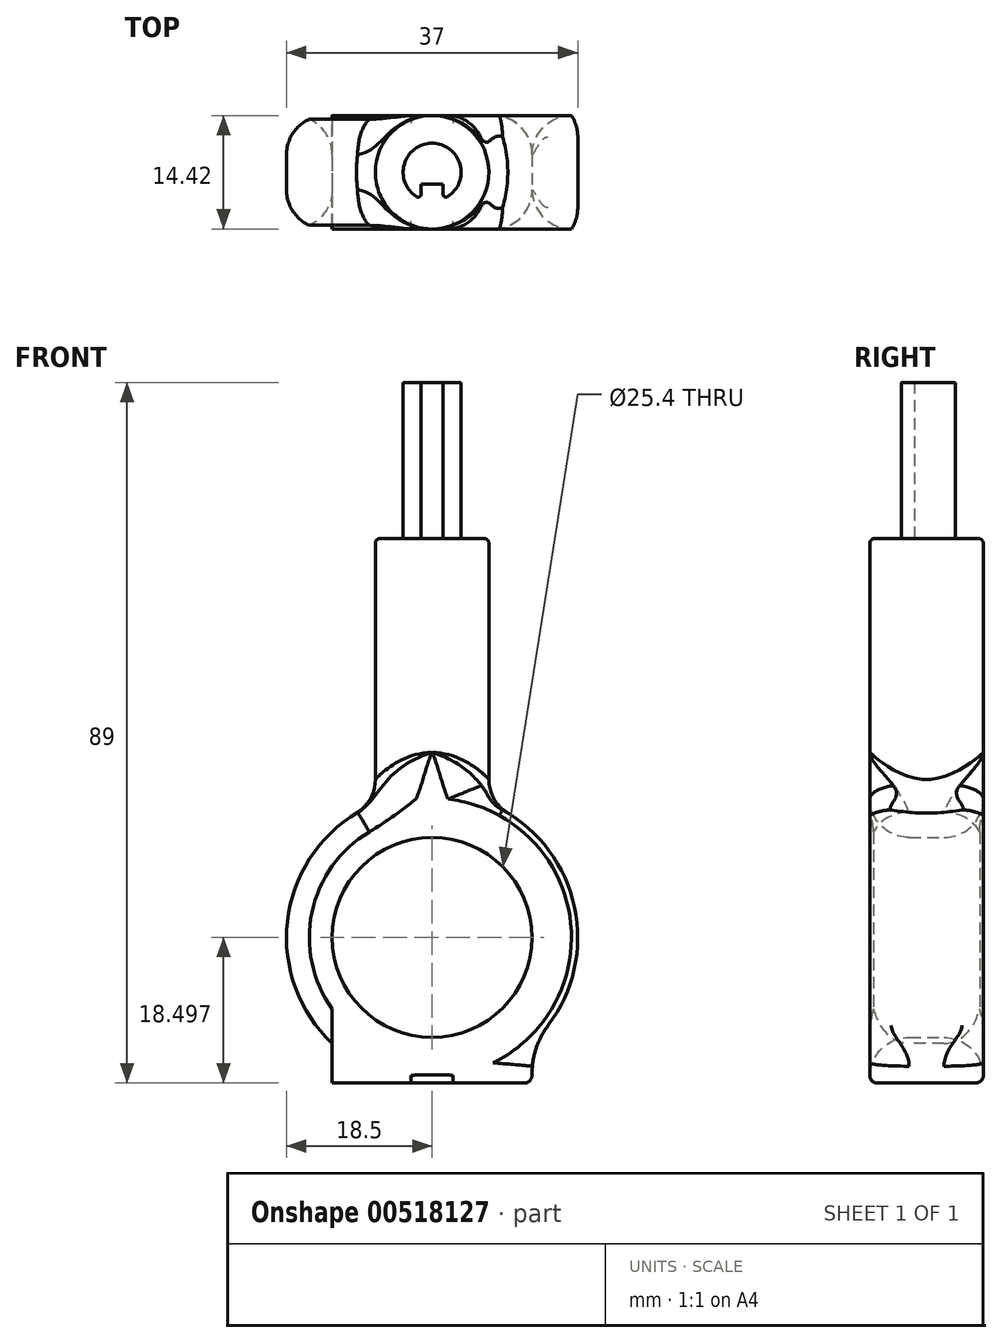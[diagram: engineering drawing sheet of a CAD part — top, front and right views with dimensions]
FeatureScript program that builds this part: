
annotation { "Feature Type Name" : "Feature", "Feature Type Description" : "" }
export const myFeature = defineFeature(function(context is Context, id is Id, definition is map)
    precondition{}
    {
        {
            var Q0;
            Q0=qCreatedBy(makeId("Top.planeOp"),FACE);
            var sketch = newSketch(context, id + "F0", { "sketchPlane" : qUnion([Q0])});
            skCircle(sketch, "E0", {"center": v(0, 0) * mm, "radius": 3.68 * mm});
            skSolve(sketch);
        }
        {
            var Q0;
            Q0 = qSketchRegion(id + "F0", true);
            extrude(context, id + "F1", {"entities" : qUnion([Q0]), "depth" : 19.8 * mm, "offsetDistance" : 25.4 * mm});
        }
        {
            var Q0;
            Q0=makeQuery(id+"F1.opExtrude","CAP_FACE",FACE,{"disambiguationData":[OSD([sQuery(id+"F0.wireOp",EDGE,"E0")])],"isStart":false});
            var sketch = newSketch(context, id + "F2", { "sketchPlane" : qUnion([Q0])});
            skLineSegment(sketch, "E1.bottom", {"start": v(-1.4, -3.68) * mm, "end": v(1.4, -3.68) * mm});
            skLineSegment(sketch, "E1.top", {"start": v(-1.4, -1.51) * mm, "end": v(1.4, -1.51) * mm});
            skLineSegment(sketch, "E1.left", {"start": v(-1.4, -3.68) * mm, "end": v(-1.4, -1.51) * mm});
            skLineSegment(sketch, "E1.right", {"start": v(1.4, -3.68) * mm, "end": v(1.4, -1.51) * mm});
            skSolve(sketch);
        }
        {
            var Q0;
            Q0 = qSketchRegion(id + "F2", true);
            extrude(context, id + "F3", {"entities" : qUnion([Q0]), "operationType" : NewBodyOperationType.REMOVE, "oppositeDirection" : true, "depth" : 25.4 * mm, "offsetDistance" : 25.4 * mm});
        }
        {
            var Q0;
            Q0=makeQuery(id+"F3.boolean.opBoolean","INTERSECT",EDGE,{"derivedFrom":[makeQuery(id+"F1.opExtrude","SWEPT_FACE",FACE,{"disambiguationData":[OSD([sQuery(id+"F0.wireOp",EDGE,"E0")])]}),makeQuery(id+"F3.opExtrude","SWEPT_FACE",FACE,{"disambiguationData":[OSD([sQuery(id+"F2.wireOp",EDGE,"E1.right")])]})]});
            var Q1;
            Q1=makeQuery(id+"F3.boolean.opBoolean","INTERSECT",EDGE,{"derivedFrom":[makeQuery(id+"F1.opExtrude","SWEPT_FACE",FACE,{"disambiguationData":[OSD([sQuery(id+"F0.wireOp",EDGE,"E0")])]}),makeQuery(id+"F3.opExtrude","SWEPT_FACE",FACE,{"disambiguationData":[OSD([sQuery(id+"F2.wireOp",EDGE,"E1.left")])]})]});
            fillet(context, id + "F4", {"entities" : qUnion([Q0, Q1]), "radius" : 0.38 * mm, "tangentPropagation" : true, "allowEdgeOverflow" : false});
        }
        {
            var Q0;
            Q0=makeQuery(id+"F1.opExtrude","CAP_FACE",FACE,{"disambiguationData":[OSD([sQuery(id+"F0.wireOp",EDGE,"E0")])],"isStart":true});
            var sketch = newSketch(context, id + "F5", { "sketchPlane" : qUnion([Q0])});
            skCircle(sketch, "E2", {"center": v(0, 0) * mm, "radius": 7.21 * mm});
            skSolve(sketch);
        }
        {
            var Q0;
            Q0 = qSketchRegion(id + "F5", true);
            extrude(context, id + "F6", {"entities" : qUnion([Q0]), "operationType" : NewBodyOperationType.ADD, "depth" : 12.7 * mm, "offsetDistance" : 25.4 * mm});
        }
        {
            var Q0;
            Q0=makeQuery(id+"F6.opExtrude","CAP_EDGE",EDGE,{"disambiguationData":[OSD([sQuery(id+"F5.wireOp",EDGE,"E2")])],"isStart":false});
            fillet(context, id + "F7", {"entities" : qUnion([Q0]), "radius" : 2.54 * mm, "tangentPropagation" : true, "allowEdgeOverflow" : false});
        }
        {
            var Q0;
            Q0=makeQuery(id+"F6.opExtrude","CAP_EDGE",EDGE,{"disambiguationData":[OSD([sQuery(id+"F5.wireOp",EDGE,"E2")])],"isStart":true});
            fillet(context, id + "F8", {"entities" : qUnion([Q0]), "radius" : 0.64 * mm, "tangentPropagation" : true, "allowEdgeOverflow" : false});
        }
        {
            var Q0;
            Q0=makeQuery(id+"F6.opExtrude","CAP_FACE",FACE,{"disambiguationData":[OSD([sQuery(id+"F5.wireOp",EDGE,"E2")])],"isStart":false});
            var sketch = newSketch(context, id + "F9", { "sketchPlane" : qUnion([Q0])});
            skCircle(sketch, "E3.0", {"center": v(0, 0) * mm, "radius": 7.21 * mm});
            skSolve(sketch);
        }
        {
            var Q0;
            Q0 = qSketchRegion(id + "F9", true);
            extrude(context, id + "F10", {"entities" : qUnion([Q0]), "operationType" : NewBodyOperationType.ADD, "depth" : 25 * mm, "offsetDistance" : 25 * mm, "hasSecondDirection" : true, "secondDirectionOppositeDirection" : true, "secondDirectionDepth" : 5 * mm});
        }
        {
            var Q0;
            Q0=qCreatedBy(makeId("Front.planeOp"),FACE);
            var sketch = newSketch(context, id + "F11", { "sketchPlane" : qUnion([Q0])});
            skCircle(sketch, "E4", {"center": v(0, -50.7) * mm, "radius": 12.7 * mm});
            skCircle(sketch, "E5", {"center": v(0, -50.7) * mm, "radius": 18.5 * mm});
            skSolve(sketch);
        }
        {
            var Q0;
            Q0 = qSketchRegion(id + "F11", true);
            extrude(context, id + "F12", {"entities" : qUnion([Q0]), "operationType" : NewBodyOperationType.ADD, "depth" : (14.43 / 2) * mm, "offsetDistance" : 25 * mm, "hasSecondDirection" : true, "secondDirectionOppositeDirection" : true, "secondDirectionDepth" : (14.43 / 2) * mm});
        }
        {
            var Q0;
            Q0=makeQuery(id+"F12.boolean.opBoolean","INTERSECT",EDGE,{"disambiguationData":[OD(1.0)],"derivedFrom":[makeQuery(id+"F10.boolean.opBoolean","MERGE",FACE,{"derivedFrom":[makeQuery(id+"F6.opExtrude","SWEPT_FACE",FACE,{"disambiguationData":[OSD([sQuery(id+"F5.wireOp",EDGE,"E2")])]}),makeQuery(id+"F10.opExtrude","SWEPT_FACE",FACE,{"disambiguationData":[OSD([sQuery(id+"F9.wireOp",EDGE,"E3.0")])]})]}),makeQuery(id+"F12.opExtrude","SWEPT_FACE",FACE,{"disambiguationData":[OSD([sQuery(id+"F11.wireOp",EDGE,"E5")])]})]});
            var Q1;
            Q1=makeQuery(id+"F12.boolean.opBoolean","INTERSECT",EDGE,{"disambiguationData":[OD(0.0)],"derivedFrom":[makeQuery(id+"F10.boolean.opBoolean","MERGE",FACE,{"derivedFrom":[makeQuery(id+"F6.opExtrude","SWEPT_FACE",FACE,{"disambiguationData":[OSD([sQuery(id+"F5.wireOp",EDGE,"E2")])]}),makeQuery(id+"F10.opExtrude","SWEPT_FACE",FACE,{"disambiguationData":[OSD([sQuery(id+"F9.wireOp",EDGE,"E3.0")])]})]}),makeQuery(id+"F12.opExtrude","SWEPT_FACE",FACE,{"disambiguationData":[OSD([sQuery(id+"F11.wireOp",EDGE,"E5")])]})]});
            fillet(context, id + "F13", {"entities" : qUnion([Q0, Q1]), "tangentPropagation" : true, "radius" : 5 * mm, "defaultsChanged" : false, "vertexSettings" : [], "allowEdgeOverflow" : false});
        }
        {
            var Q0;
            Q0=makeQuery(id+"F12.opExtrude","CAP_FACE",FACE,{"disambiguationData":[OSD([sQuery(id+"F11.wireOp",EDGE,"E4"),sQuery(id+"F11.wireOp",EDGE,"E5")])],"isStart":false});
            var sketch = newSketch(context, id + "F14", { "sketchPlane" : qUnion([Q0])});
            skLineSegment(sketch, "E6", {"start": v(-12.7, -64.15) * mm, "end": v(-12.7, -69.2) * mm});
            skLineSegment(sketch, "E7", {"start": v(-12.7, -69.2) * mm, "end": v(12.7, -69.2) * mm});
            skLineSegment(sketch, "E8", {"start": v(12.7, -69.2) * mm, "end": v(12.7, -64.15) * mm});
            skLineSegment(sketch, "E9", {"start": v(12.7, -64.15) * mm, "end": v(5.8, -66.72) * mm});
            skLineSegment(sketch, "E10", {"start": v(5.8, -66.72) * mm, "end": v(-3.07, -66.72) * mm});
            skLineSegment(sketch, "E11", {"start": v(-3.07, -66.72) * mm, "end": v(-12.7, -64.15) * mm});
            skSolve(sketch);
        }
        {
            var Q0;
            Q0 = qSketchRegion(id + "F14", true);
            extrude(context, id + "F15", {"entities" : qUnion([Q0]), "operationType" : NewBodyOperationType.ADD, "oppositeDirection" : true, "depth" : 14.43 * mm, "offsetDistance" : 25 * mm});
        }
        {
            var Q0;
            Q0=makeQuery(id+"F15.opExtrude","SWEPT_EDGE",EDGE,{"disambiguationData":[OSD([sQuery(id+"F11.wireOp",EDGE,"E5"),sQuery(id+"F14.wireOp",EDGE,"E8"),sQuery(id+"F14.wireOp",EDGE,"E9")])]});
            var Q1;
            Q1=makeQuery(id+"F15.opExtrude","SWEPT_EDGE",EDGE,{"disambiguationData":[OSD([sQuery(id+"F11.wireOp",EDGE,"E5"),sQuery(id+"F14.wireOp",EDGE,"E6"),sQuery(id+"F14.wireOp",EDGE,"E11")])]});
            fillet(context, id + "F16", {"entities" : qUnion([Q0, Q1]), "tangentPropagation" : true, "radius" : 10 * mm, "defaultsChanged" : true, "vertexSettings" : [], "allowEdgeOverflow" : false});
        }
        {
            var Q0;
            Q0=makeQuery(id+"F12.opExtrude","CAP_EDGE",EDGE,{"disambiguationData":[OSD([sQuery(id+"F11.wireOp",EDGE,"E4")])],"isStart":false});
            fillet(context, id + "F17", {"entities" : qUnion([Q0]), "tangentPropagation" : true, "radius" : 5 * mm, "defaultsChanged" : false, "vertexSettings" : [], "allowEdgeOverflow" : false});
        }
        {
            var Q0;
            Q0=makeQuery(id+"F12.opExtrude","CAP_EDGE",EDGE,{"disambiguationData":[OSD([sQuery(id+"F11.wireOp",EDGE,"E4")])],"isStart":true});
            fillet(context, id + "F18", {"entities" : qUnion([Q0]), "tangentPropagation" : true, "radius" : 5 * mm, "defaultsChanged" : false, "vertexSettings" : [], "allowEdgeOverflow" : false});
        }
        {
            var Q0;
            {var subQ0=sQuery(id+"F14.wireOp",EDGE,"E6");var subQ1=sQuery(id+"F11.wireOp",EDGE,"E5");Q0=makeQuery(id+"F15.boolean.opBoolean","SPLIT",EDGE,{"disambiguationData":[TD([makeQuery(id+"F15.opExtrude","SWEPT_FACE",FACE,{"disambiguationData":[OSD([subQ0])]})])],"derivedFrom":makeQuery(id+"F12.opExtrude","CAP_EDGE",EDGE,{"disambiguationData":[OSD([subQ1])],"isStart":false})});}
            var Q1;
            {var subQ0=sQuery(id+"F14.wireOp",EDGE,"E6");var subQ1=sQuery(id+"F11.wireOp",EDGE,"E5");Q1=makeQuery(id+"F15.boolean.opBoolean","SPLIT",EDGE,{"disambiguationData":[TD([makeQuery(id+"F15.opExtrude","SWEPT_FACE",FACE,{"disambiguationData":[OSD([subQ0])]})])],"derivedFrom":makeQuery(id+"F12.opExtrude","CAP_EDGE",EDGE,{"disambiguationData":[OSD([subQ1])],"isStart":true})});}
            var Q2;
            {var subQ0=sQuery(id+"F14.wireOp",EDGE,"E8");var subQ1=sQuery(id+"F11.wireOp",EDGE,"E5");Q2=makeQuery(id+"F15.boolean.opBoolean","SPLIT",EDGE,{"disambiguationData":[TD([makeQuery(id+"F15.opExtrude","SWEPT_FACE",FACE,{"disambiguationData":[OSD([subQ0])]})])],"derivedFrom":makeQuery(id+"F12.opExtrude","CAP_EDGE",EDGE,{"disambiguationData":[OSD([subQ1])],"isStart":false})});}
            var Q3;
            {var subQ0=sQuery(id+"F14.wireOp",EDGE,"E8");var subQ1=sQuery(id+"F11.wireOp",EDGE,"E5");Q3=makeQuery(id+"F15.boolean.opBoolean","SPLIT",EDGE,{"disambiguationData":[TD([makeQuery(id+"F15.opExtrude","SWEPT_FACE",FACE,{"disambiguationData":[OSD([subQ0])]})])],"derivedFrom":makeQuery(id+"F12.opExtrude","CAP_EDGE",EDGE,{"disambiguationData":[OSD([subQ1])],"isStart":true})});}
            fillet(context, id + "F19", {"entities" : qUnion([Q0, Q1, Q2, Q3]), "tangentPropagation" : true, "radius" : 5 * mm, "defaultsChanged" : false, "vertexSettings" : [], "allowEdgeOverflow" : false});
        }
        {
            var Q0;
            Q0=makeQuery(id+"F15.opExtrude","CAP_EDGE",EDGE,{"disambiguationData":[OSD([sQuery(id+"F14.wireOp",EDGE,"E7")])],"isStart":true});
            fillet(context, id + "F20", {"entities" : qUnion([Q0]), "tangentPropagation" : true, "radius" : 1 * mm, "defaultsChanged" : true, "vertexSettings" : [], "allowEdgeOverflow" : false});
        }
    });
